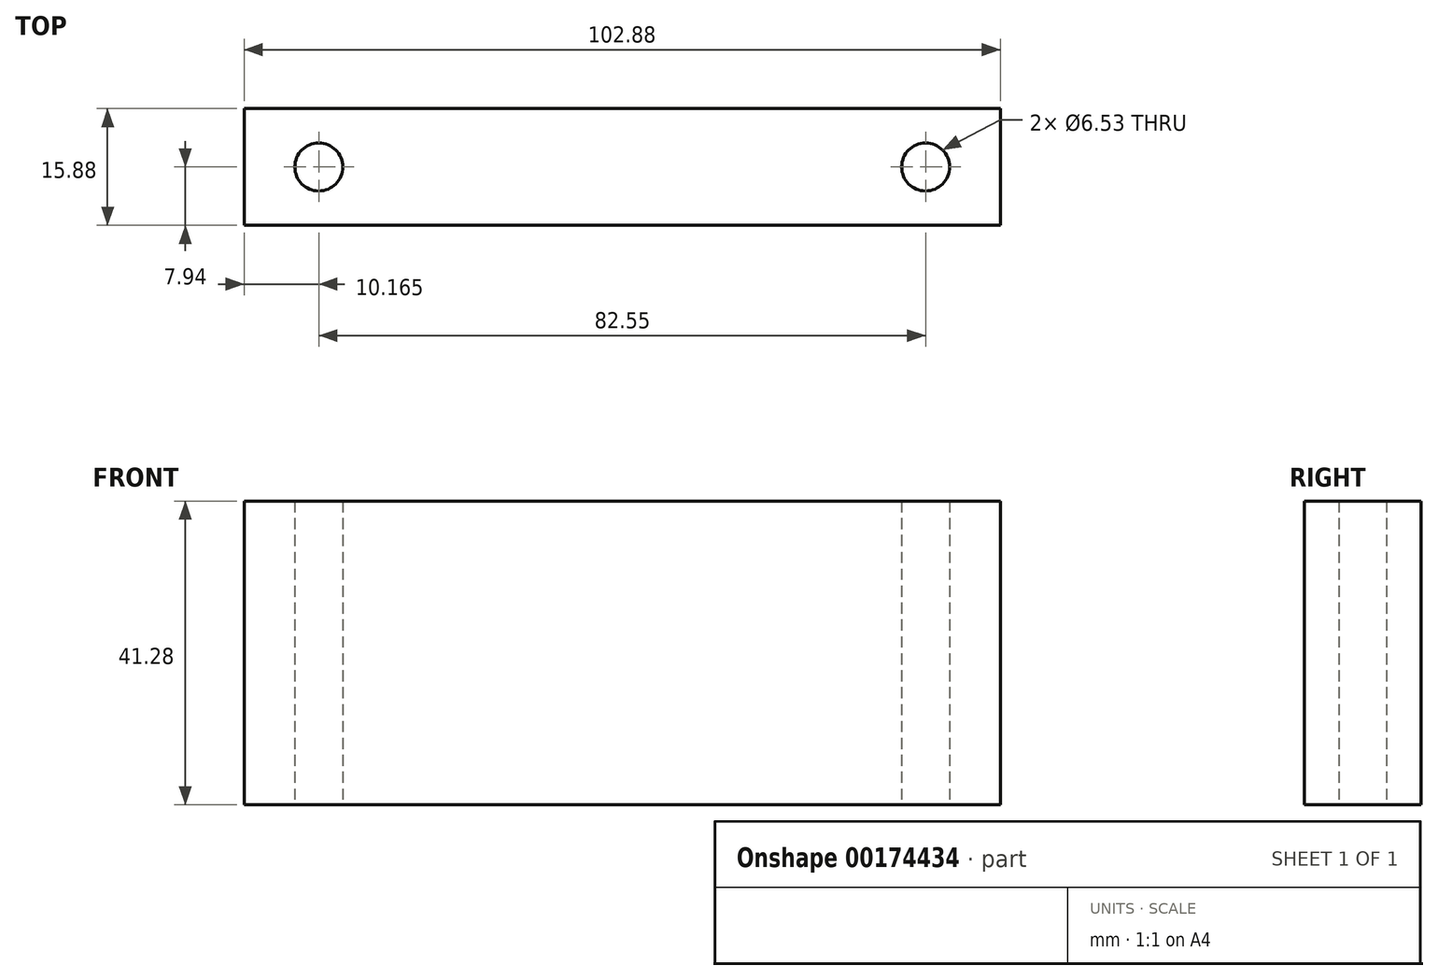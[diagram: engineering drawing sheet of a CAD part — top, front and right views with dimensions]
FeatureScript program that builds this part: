
annotation { "Feature Type Name" : "Feature", "Feature Type Description" : "" }
export const myFeature = defineFeature(function(context is Context, id is Id, definition is map)
    precondition{}
    {
        {
            var Q0;
            Q0=qCreatedBy(makeId("Top.planeOp"),FACE);
            var sketch = newSketch(context, id + "F0", { "sketchPlane" : qUnion([Q0])});
            skLineSegment(sketch, "E0.bottom", {"start": v(-51.44, 7.94) * mm, "end": v(51.44, 7.94) * mm});
            skLineSegment(sketch, "E0.top", {"start": v(-51.44, -7.94) * mm, "end": v(51.44, -7.94) * mm});
            skLineSegment(sketch, "E0.left", {"start": v(-51.44, 7.94) * mm, "end": v(-51.44, -7.94) * mm});
            skLineSegment(sketch, "E0.right", {"start": v(51.44, 7.94) * mm, "end": v(51.44, -7.94) * mm});
            skPoint(sketch, "E0.middle", {"position": v(0, 0) * mm});
            skCircle(sketch, "E1", {"center": v(-41.28, 0) * mm, "radius": 3.26 * mm});
            skCircle(sketch, "E2", {"center": v(41.28, 0) * mm, "radius": 3.26 * mm});
            skSolve(sketch);
        }
        {
            var Q0;
            Q0=makeQuery(id+"F0.imprint","IMPRINT",FACE,{"disambiguationData":[TD([[makeQuery(id+"F0.imprint","IMPRINT",EDGE,{"derivedFrom":sQuery(id+"F0.wireOp",EDGE,"E0.bottom")}),-1.0]])]});
            extrude(context, id + "F1", {"entities" : qUnion([Q0]), "depth" : 41.27 * mm});
        }
    });
